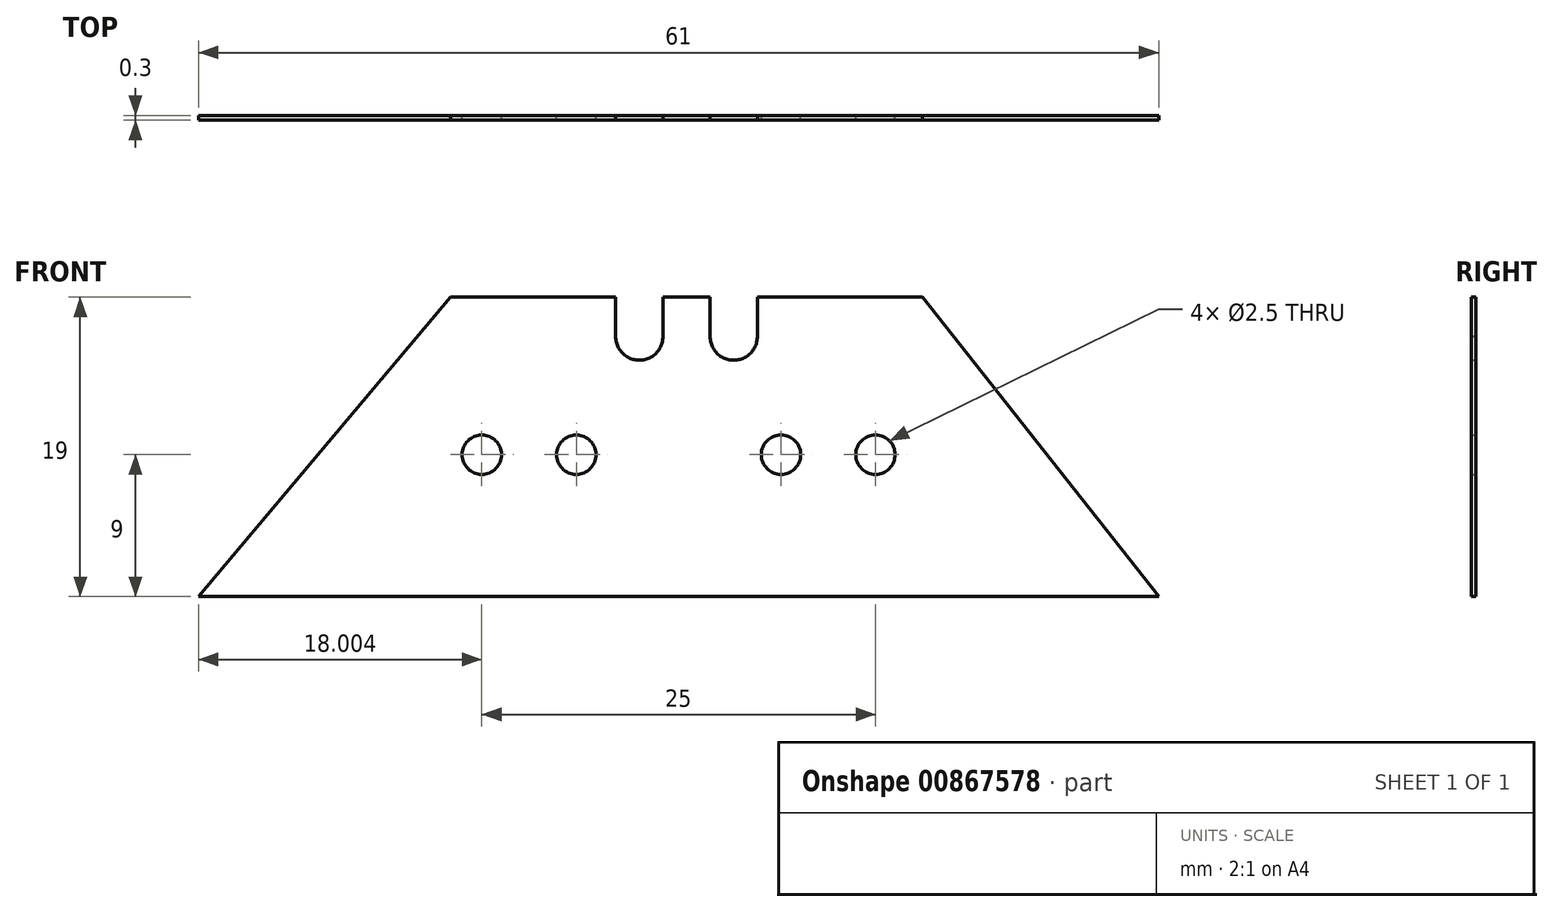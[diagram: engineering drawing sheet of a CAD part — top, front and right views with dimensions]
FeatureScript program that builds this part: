
annotation { "Feature Type Name" : "Feature", "Feature Type Description" : "" }
export const myFeature = defineFeature(function(context is Context, id is Id, definition is map)
    precondition{}
    {
        {
            var Q0;
            Q0=qCreatedBy(makeId("Front.planeOp"),FACE);
            var sketch = newSketch(context, id + "F0", { "sketchPlane" : qUnion([Q0])});
            skLineSegment(sketch, "E0", {"start": v(0.01, 0) * mm, "end": v(61.01, 0) * mm});
            skPoint(sketch, "E1", {"position": v(31.01, 19) * mm});
            skPoint(sketch, "E2", {"position": v(46.01, 19) * mm});
            skPoint(sketch, "E3", {"position": v(16.01, 19) * mm});
            skLineSegment(sketch, "E4", {"start": v(46.01, 19) * mm, "end": v(61.01, 0) * mm});
            skLineSegment(sketch, "E5", {"start": v(46.01, 19) * mm, "end": v(35.51, 19) * mm});
            skLineSegment(sketch, "E6", {"start": v(16.01, 19) * mm, "end": v(0.01, 0) * mm});
            skPoint(sketch, "E7", {"position": v(34.01, 16.5) * mm});
            skPoint(sketch, "E8", {"position": v(28.01, 16.5) * mm});
            skArc(sketch, "E9", {"start": v(26.51, 16.52) * mm, "mid": v(28, 15) * mm, "end": v(29.51, 16.5) * mm});
            skArc(sketch, "E10", {"start": v(32.51, 16.5) * mm, "mid": v(34.03, 15) * mm, "end": v(35.51, 16.55) * mm});
            skLineSegment(sketch, "E11", {"start": v(29.51, 16.5) * mm, "end": v(29.51, 19) * mm});
            skLineSegment(sketch, "E12", {"start": v(35.51, 16.55) * mm, "end": v(35.51, 19) * mm});
            skLineSegment(sketch, "E13", {"start": v(32.51, 16.5) * mm, "end": v(32.51, 19) * mm});
            skLineSegment(sketch, "E14", {"start": v(26.51, 16.52) * mm, "end": v(26.51, 19) * mm});
            skLineSegment(sketch, "E15.trimOffspring", {"start": v(26.51, 19) * mm, "end": v(16.01, 19) * mm});
            skLineSegment(sketch, "E16.trimOffspring", {"start": v(32.51, 19) * mm, "end": v(29.51, 19) * mm});
            skPoint(sketch, "E17", {"position": v(43.01, 9) * mm});
            skPoint(sketch, "E18", {"position": v(37.01, 9) * mm});
            skPoint(sketch, "E19", {"position": v(18.01, 9) * mm});
            skPoint(sketch, "E20", {"position": v(24.01, 9) * mm});
            skCircle(sketch, "E21", {"center": v(18.01, 9) * mm, "radius": 1.25 * mm});
            skCircle(sketch, "E22", {"center": v(24.01, 9) * mm, "radius": 1.25 * mm});
            skCircle(sketch, "E23", {"center": v(37.01, 9) * mm, "radius": 1.25 * mm});
            skCircle(sketch, "E24", {"center": v(43.01, 9) * mm, "radius": 1.25 * mm});
            skLineSegment(sketch, "E25", {"start": v(26.51, 16.52) * mm, "end": v(26.51, 0) * mm});
            skLineSegment(sketch, "E26", {"start": v(35.51, 16.55) * mm, "end": v(35.51, 0) * mm});
            skSolve(sketch);
        }
        {
            var Q0;
            Q0=makeQuery(id+"F0.imprint","IMPRINT",FACE,{"disambiguationData":[TD([[makeQuery(id+"F0.imprint","IMPRINT",EDGE,{"derivedFrom":sQuery(id+"F0.wireOp",EDGE,"E0")}),1.0]])]});
            extrude(context, id + "F1", {"entities" : qUnion([Q0]), "depth" : 0.3 * mm, "offsetDistance" : 25 * mm});
        }
    });
